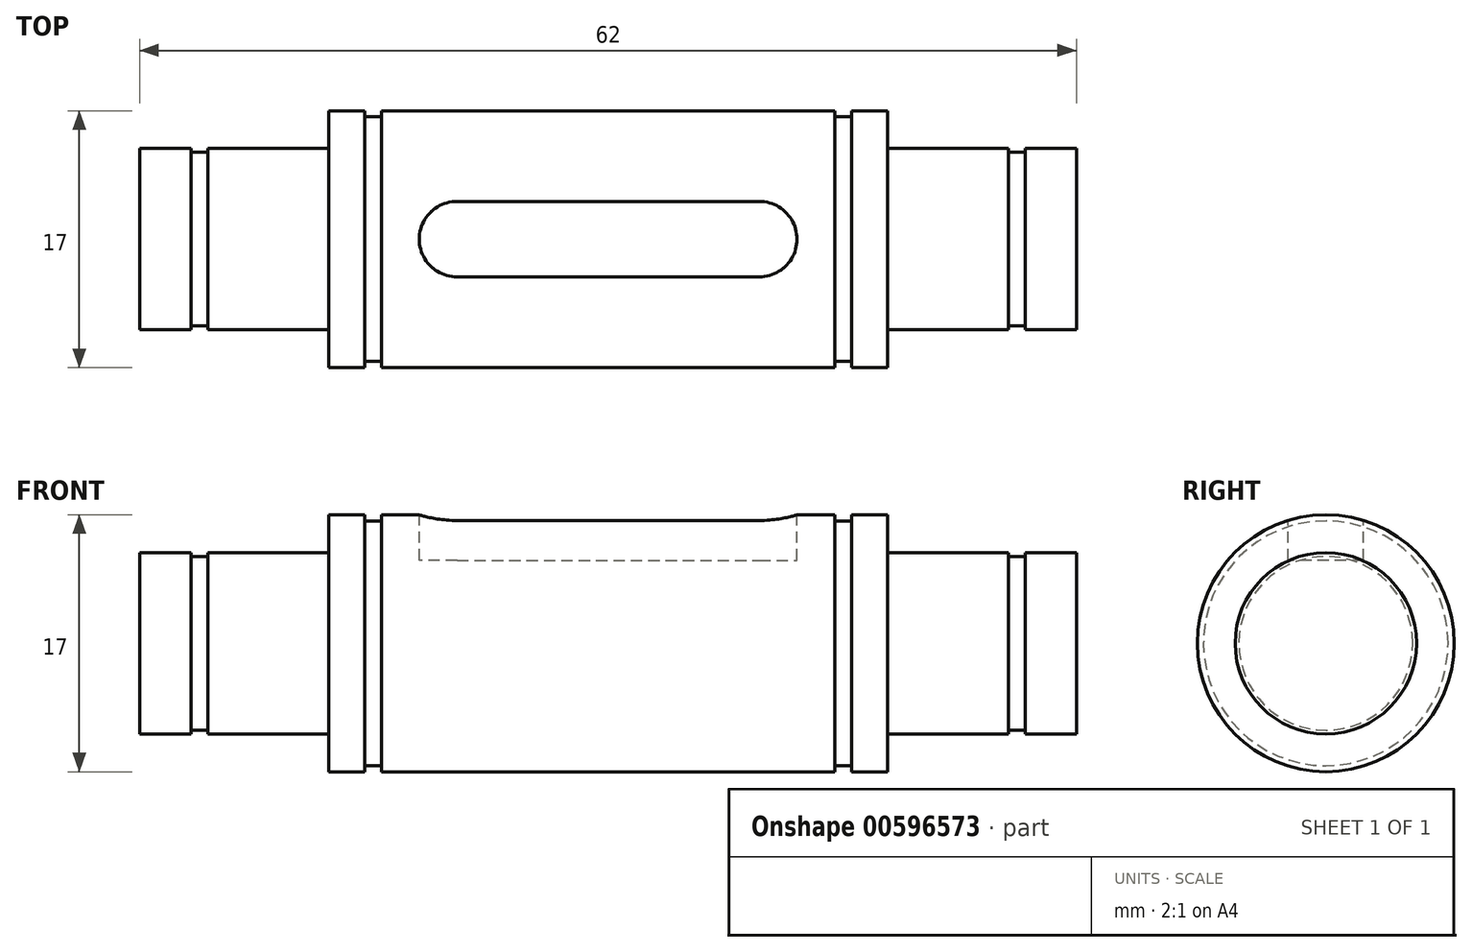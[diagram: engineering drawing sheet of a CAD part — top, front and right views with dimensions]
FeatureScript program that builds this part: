
annotation { "Feature Type Name" : "Feature", "Feature Type Description" : "" }
export const myFeature = defineFeature(function(context is Context, id is Id, definition is map)
    precondition{}
    {
        {
            var Q0;
            Q0=qCreatedBy(makeId("Front.planeOp"),FACE);
            var sketch = newSketch(context, id + "F0", { "sketchPlane" : qUnion([Q0])});
            skLineSegment(sketch, "E0", {"start": v(2.25, 0) * mm, "end": v(64.25, 0) * mm});
            skLineSegment(sketch, "E1", {"start": v(64.25, 0) * mm, "end": v(64.25, 6) * mm});
            skLineSegment(sketch, "E2", {"start": v(64.25, 6) * mm, "end": v(60.85, 6) * mm});
            skLineSegment(sketch, "E3", {"start": v(51.75, 6) * mm, "end": v(51.75, 8.5) * mm});
            skLineSegment(sketch, "E4", {"start": v(51.75, 8.5) * mm, "end": v(49.35, 8.5) * mm});
            skLineSegment(sketch, "E5", {"start": v(49.35, 8.5) * mm, "end": v(49.35, 8.1) * mm});
            skLineSegment(sketch, "E6", {"start": v(49.35, 8.1) * mm, "end": v(48.25, 8.1) * mm});
            skLineSegment(sketch, "E7", {"start": v(48.25, 8.1) * mm, "end": v(48.25, 8.5) * mm});
            skLineSegment(sketch, "E8", {"start": v(48.25, 8.5) * mm, "end": v(18.25, 8.5) * mm});
            skLineSegment(sketch, "E9", {"start": v(18.25, 8.5) * mm, "end": v(18.25, 8.1) * mm});
            skLineSegment(sketch, "E10", {"start": v(18.25, 8.1) * mm, "end": v(17.15, 8.1) * mm});
            skLineSegment(sketch, "E11", {"start": v(17.15, 8.1) * mm, "end": v(17.15, 8.5) * mm});
            skLineSegment(sketch, "E12", {"start": v(17.15, 8.5) * mm, "end": v(14.75, 8.5) * mm});
            skLineSegment(sketch, "E13", {"start": v(14.75, 8.5) * mm, "end": v(14.75, 6) * mm});
            skLineSegment(sketch, "E14", {"start": v(14.75, 6) * mm, "end": v(6.75, 6) * mm});
            skLineSegment(sketch, "E15", {"start": v(6.75, 6) * mm, "end": v(6.75, 5.75) * mm});
            skLineSegment(sketch, "E16", {"start": v(6.75, 5.75) * mm, "end": v(5.65, 5.75) * mm});
            skLineSegment(sketch, "E17", {"start": v(5.65, 5.75) * mm, "end": v(5.65, 6) * mm});
            skLineSegment(sketch, "E18", {"start": v(5.65, 6) * mm, "end": v(2.25, 6) * mm});
            skLineSegment(sketch, "E19", {"start": v(2.25, 6) * mm, "end": v(2.25, 0) * mm});
            skLineSegment(sketch, "E20", {"start": v(59.75, 5.75) * mm, "end": v(60.85, 5.75) * mm});
            skLineSegment(sketch, "E21", {"start": v(59.75, 5.75) * mm, "end": v(59.75, 6) * mm});
            skLineSegment(sketch, "E22", {"start": v(60.85, 5.75) * mm, "end": v(60.85, 6) * mm});
            skLineSegment(sketch, "E23.trimOffspring", {"start": v(59.75, 6) * mm, "end": v(51.75, 6) * mm});
            skSolve(sketch);
        }
        {
            var Q0;
            Q0=makeQuery(id+"F0.imprint","IMPRINT",FACE,{"disambiguationData":[TD([[makeQuery(id+"F0.imprint","IMPRINT",EDGE,{"derivedFrom":sQuery(id+"F0.wireOp",EDGE,"E0")}),1.0]])]});
            var Q1;
            Q1=sQuery(id+"F0.wireOp",EDGE,"E0");
            revolve(context, id + "F1", {"entities" : qUnion([Q0]), "axis" : qUnion([Q1]), "revolveType" : RevolveType.FULL});
        }
        {
            var Q0;
            Q0=qCreatedBy(makeId("Top.planeOp"),FACE);
            cPlane(context, id + "F2", {"entities" : qUnion([Q0]), "cplaneType" : CPlaneType.OFFSET, "offset" : (17 / 2) * mm, "width" : 150 * mm, "height" : 150 * mm});
        }
        {
            var Q0;
            Q0=qCreatedBy(id+"F2.planeOp",FACE);
            var sketch = newSketch(context, id + "F3", { "sketchPlane" : qUnion([Q0])});
            skArc(sketch, "E24", {"start": v(23.25, 2.5) * mm, "mid": v(20.75, 0) * mm, "end": v(23.25, -2.5) * mm});
            skArc(sketch, "E25", {"start": v(43.25, -2.5) * mm, "mid": v(45.75, 0) * mm, "end": v(43.25, 2.5) * mm});
            skLineSegment(sketch, "E26", {"start": v(23.25, 2.5) * mm, "end": v(43.25, 2.5) * mm});
            skLineSegment(sketch, "E27", {"start": v(23.25, -2.5) * mm, "end": v(43.25, -2.5) * mm});
            skSolve(sketch);
        }
        {
            var Q0;
            Q0=makeQuery(id+"F3.imprint","IMPRINT",FACE,{"disambiguationData":[TD([[makeQuery(id+"F3.imprint","IMPRINT",EDGE,{"derivedFrom":sQuery(id+"F3.wireOp",EDGE,"E24")}),1.0]])]});
            extrude(context, id + "F4", {"entities" : qUnion([Q0]), "operationType" : NewBodyOperationType.REMOVE, "oppositeDirection" : true, "depth" : 3 * mm, "offsetDistance" : 25 * mm});
        }
    });
